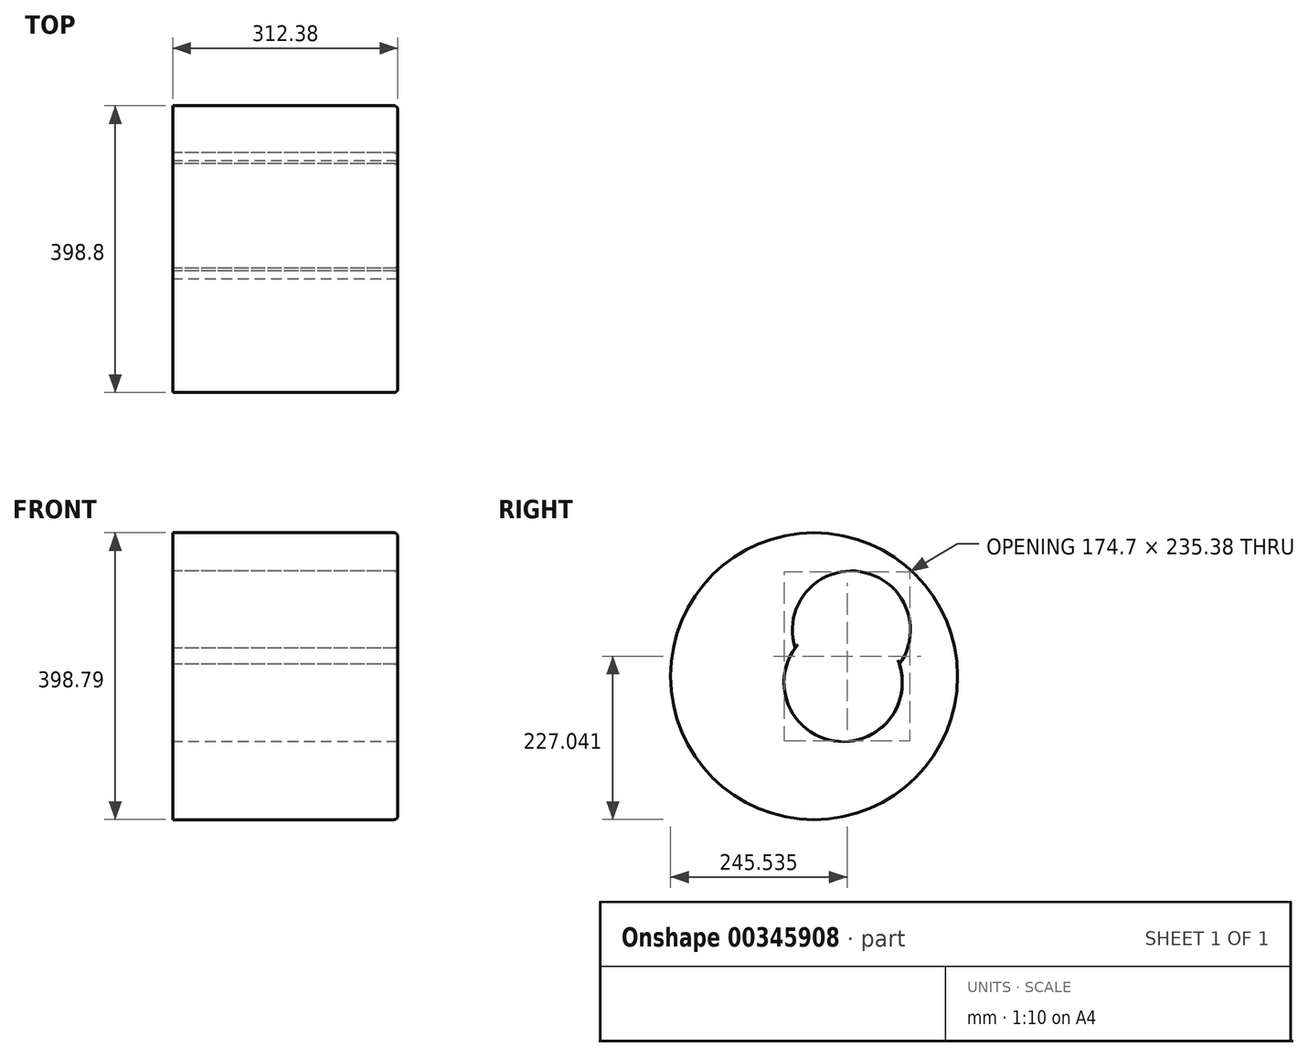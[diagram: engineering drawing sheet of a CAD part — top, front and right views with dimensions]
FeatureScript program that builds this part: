
annotation { "Feature Type Name" : "Feature", "Feature Type Description" : "" }
export const myFeature = defineFeature(function(context is Context, id is Id, definition is map)
    precondition{}
    {
        {
            var Q0;
            Q0=qCreatedBy(makeId("Right.planeOp"),FACE);
            var sketch = newSketch(context, id + "F0", { "sketchPlane" : qUnion([Q0])});
            skCircle(sketch, "E0", {"center": v(0, 0) * mm, "radius": 21.23 * mm});
            skCircle(sketch, "E1", {"center": v(0, 0) * mm, "radius": 13.55 * mm});
            skCircle(sketch, "E2", {"center": v(-33.93, -38.37) * mm, "radius": 82.25 * mm});
            skCircle(sketch, "E3", {"center": v(-22.54, 34.64) * mm, "radius": 82.08 * mm});
            skCircle(sketch, "E4", {"center": v(-74.44, -29.6) * mm, "radius": 199.4 * mm});
            skSolve(sketch);
        }
        {
            var Q0;
            Q0=makeQuery(id+"F0.imprint","IMPRINT",FACE,{"disambiguationData":[TD([[makeQuery(id+"F0.imprint","IMPRINT",EDGE,{"derivedFrom":sQuery(id+"F0.wireOp",EDGE,"E4")}),1.0]])]});
            var sketch = newSketch(context, id + "F1", { "sketchPlane" : qUnion([Q0])});
            skSolve(sketch);
        }
        {
            var Q0;
            Q0 = qSketchRegion(id + "F1", true);
            var Q1;
            Q1=makeQuery(id+"F0.imprint","IMPRINT",FACE,{"disambiguationData":[TD([[makeQuery(id+"F0.imprint","IMPRINT",EDGE,{"derivedFrom":sQuery(id+"F0.wireOp",EDGE,"E4")}),1.0]])]});
            var Q2;
            {var subQ0=sQuery(id+"F0.wireOp",EDGE,"E3");var subQ1=sQuery(id+"F0.wireOp",EDGE,"E2");var subQ2=makeQuery(id+"F0.imprint","INTERSECT",VERTEX,{"disambiguationData":[OD(0.0)],"derivedFrom":[subQ1,subQ0]});Q2=makeQuery(id+"F1.imprint","IMPRINT",FACE,{"disambiguationData":[TD([[makeQuery(id+"F1.imprint","IMPRINT",EDGE,{"derivedFrom":makeQuery(id+"F0.imprint","IMPRINT",EDGE,{"disambiguationData":[TD([[subQ2,-1.0]])],"derivedFrom":subQ1})}),1.0]])]});}
            extrude(context, id + "F2", {"entities" : qUnion([Q0, Q1, Q2]), "depth" : 312.38 * mm});
        }
        {
            var Q0;
            {var subQ0=sQuery(id+"F0.wireOp",EDGE,"E3");var subQ1=sQuery(id+"F0.wireOp",EDGE,"E2");Q0=makeQuery(id+"F2.opExtrude","CAP_EDGE",EDGE,{"disambiguationData":[OSD([subQ0]),TDD([makeQuery(id+"F1.imprint","IMPRINT",EDGE,{"derivedFrom":makeQuery(id+"F0.imprint","IMPRINT",EDGE,{"disambiguationData":[TD([[makeQuery(id+"F0.imprint","INTERSECT",VERTEX,{"disambiguationData":[OD(0.0)],"derivedFrom":[subQ1,subQ0]}),1.0]])],"derivedFrom":subQ0})})])],"isStart":false});}
            fillet(context, id + "F3", {"entities" : qUnion([Q0]), "radius" : 5.08 * mm, "tangentPropagation" : true, "allowEdgeOverflow" : false});
        }
        {
            var Q0;
            Q0=makeQuery(id+"F2.opExtrude","CAP_EDGE",EDGE,{"disambiguationData":[OSD([sQuery(id+"F0.wireOp",EDGE,"E4")])],"isStart":false});
            fillet(context, id + "F4", {"entities" : qUnion([Q0]), "radius" : 5.08 * mm, "tangentPropagation" : true, "allowEdgeOverflow" : false});
        }
    });
